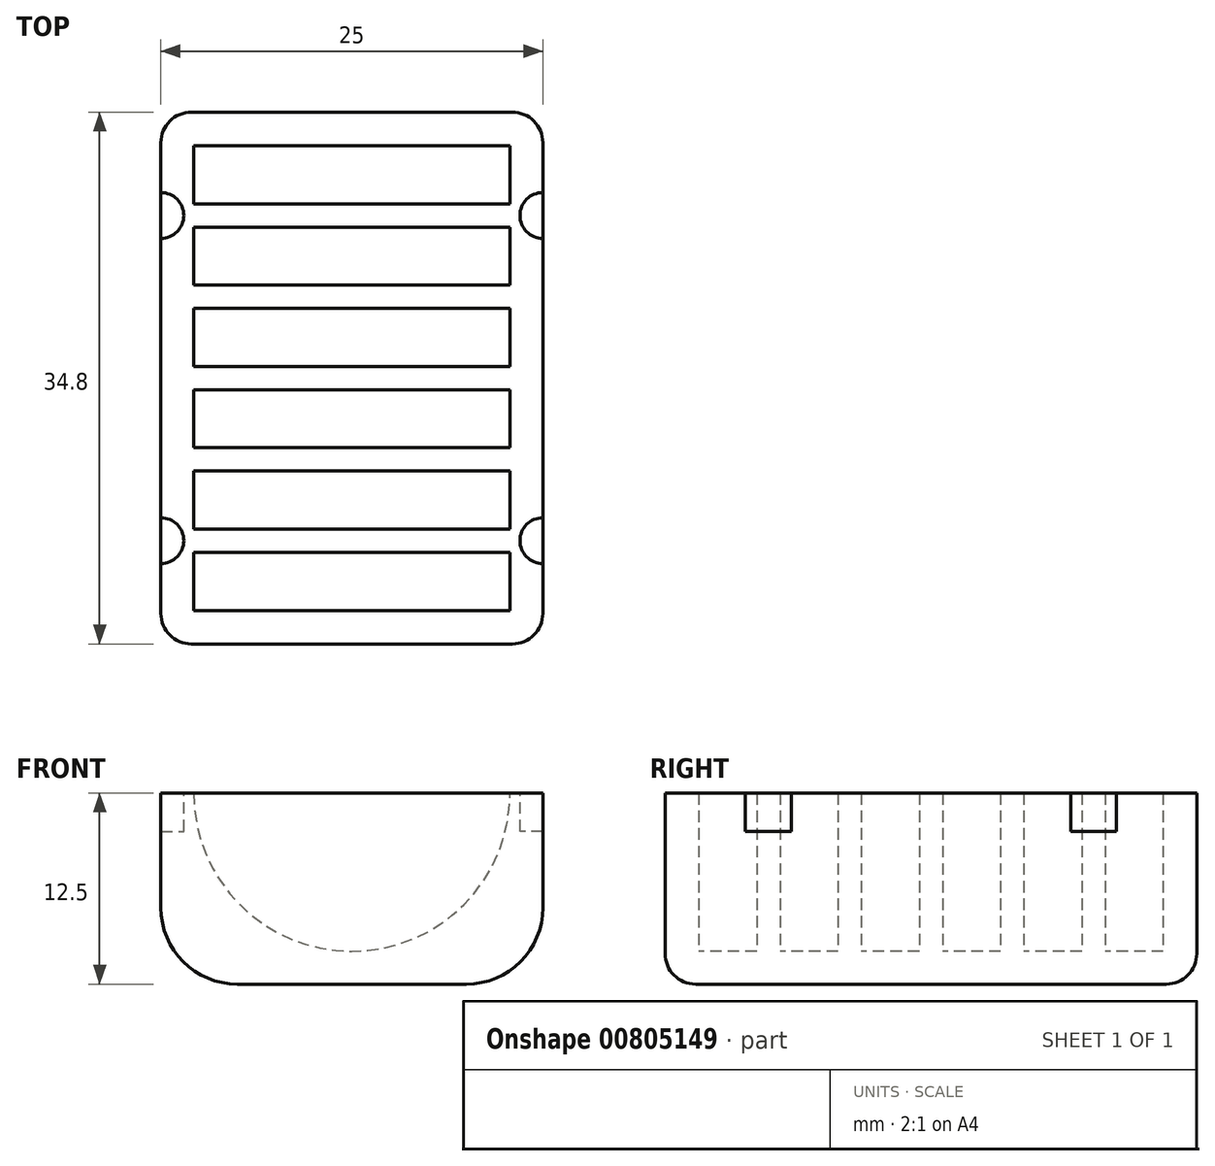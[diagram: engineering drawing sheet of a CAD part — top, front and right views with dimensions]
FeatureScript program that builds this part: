
annotation { "Feature Type Name" : "Feature", "Feature Type Description" : "" }
export const myFeature = defineFeature(function(context is Context, id is Id, definition is map)
    precondition{}
    {
        {
            var Q0;
            Q0=qCreatedBy(makeId("Top.planeOp"),FACE);
            var sketch = newSketch(context, id + "F0", { "sketchPlane" : qUnion([Q0])});
            skLineSegment(sketch, "E0.bottom", {"start": v(-30.1, 7.68) * mm, "end": v(-5.1, 7.68) * mm});
            skLineSegment(sketch, "E0.top", {"start": v(-30.1, -27.12) * mm, "end": v(-5.1, -27.12) * mm});
            skLineSegment(sketch, "E0.left", {"start": v(-30.1, 7.68) * mm, "end": v(-30.1, -27.12) * mm});
            skLineSegment(sketch, "E0.right", {"start": v(-5.1, 7.68) * mm, "end": v(-5.1, -27.12) * mm});
            skSolve(sketch);
        }
        {
            var Q0;
            Q0=qSketchRegion(id+"F0",true);
            extrude(context, id + "F1", {"entities" : qUnion([Q0]), "depth" : (25 / 2) * mm, "offsetDistance" : 25 * mm});
        }
        {
            var Q0;
            Q0=makeQuery(id+"F1.opExtrude","SWEPT_FACE",FACE,{"disambiguationData":[OSD([sQuery(id+"F0.wireOp",EDGE,"E0.top")])]});
            var sketch = newSketch(context, id + "F2", { "sketchPlane" : qUnion([Q0])});
            skCircle(sketch, "E1", {"center": v(-17.6, 12.5) * mm, "radius": 10.35 * mm});
            skSolve(sketch);
        }
        {
            var Q0;
            Q0=qSketchRegion(id+"F2",true);
            extrude(context, id + "F3", {"entities" : qUnion([Q0]), "operationType" : NewBodyOperationType.REMOVE, "oppositeDirection" : true, "depth" : (34.8 - 2.2) * mm, "offsetDistance" : 25 * mm, "hasSecondDirection" : true, "secondDirectionOppositeDirection" : true, "secondDirectionDepth" : (2.2) * mm});
        }
        {
            var Q0;
            Q0=makeQuery(id+"F1.opExtrude","CAP_FACE",FACE,{"disambiguationData":[OSD([sQuery(id+"F0.wireOp",EDGE,"E0.bottom"),sQuery(id+"F0.wireOp",EDGE,"E0.top"),sQuery(id+"F0.wireOp",EDGE,"E0.left"),sQuery(id+"F0.wireOp",EDGE,"E0.right")])],"isStart":false});
            var sketch = newSketch(context, id + "F4", { "sketchPlane" : qUnion([Q0])});
            skLineSegment(sketch, "E2.bottom", {"start": v(-27.95, 1.68) * mm, "end": v(-7.25, 1.68) * mm});
            skLineSegment(sketch, "E2.top", {"start": v(-27.95, 0.16) * mm, "end": v(-7.25, 0.16) * mm});
            skLineSegment(sketch, "E2.left", {"start": v(-27.95, 1.68) * mm, "end": v(-27.95, 0.16) * mm});
            skLineSegment(sketch, "E2.right", {"start": v(-7.25, 1.68) * mm, "end": v(-7.25, 0.16) * mm});
            skLineSegment(sketch, "E3.bottom", {"start": v(-27.95, -3.64) * mm, "end": v(-7.25, -3.64) * mm});
            skLineSegment(sketch, "E3.top", {"start": v(-27.95, -5.16) * mm, "end": v(-7.25, -5.16) * mm});
            skLineSegment(sketch, "E3.left", {"start": v(-27.95, -3.64) * mm, "end": v(-27.95, -5.16) * mm});
            skLineSegment(sketch, "E3.right", {"start": v(-7.25, -3.64) * mm, "end": v(-7.25, -5.16) * mm});
            skLineSegment(sketch, "E4.bottom", {"start": v(-27.95, -8.96) * mm, "end": v(-7.25, -8.96) * mm});
            skLineSegment(sketch, "E4.top", {"start": v(-27.95, -10.48) * mm, "end": v(-7.25, -10.48) * mm});
            skLineSegment(sketch, "E4.left", {"start": v(-27.95, -8.96) * mm, "end": v(-27.95, -10.48) * mm});
            skLineSegment(sketch, "E4.right", {"start": v(-7.25, -8.96) * mm, "end": v(-7.25, -10.48) * mm});
            skLineSegment(sketch, "E5.bottom", {"start": v(-27.95, -14.28) * mm, "end": v(-7.25, -14.28) * mm});
            skLineSegment(sketch, "E5.top", {"start": v(-27.95, -15.8) * mm, "end": v(-7.25, -15.8) * mm});
            skLineSegment(sketch, "E5.left", {"start": v(-27.95, -14.28) * mm, "end": v(-27.95, -15.8) * mm});
            skLineSegment(sketch, "E5.right", {"start": v(-7.25, -14.28) * mm, "end": v(-7.25, -15.8) * mm});
            skLineSegment(sketch, "E6.top", {"start": v(-27.95, -21.12) * mm, "end": v(-7.25, -21.12) * mm});
            skLineSegment(sketch, "E7", {"start": v(-27.95, -21.12) * mm, "end": v(-27.95, -19.6) * mm});
            skLineSegment(sketch, "E8", {"start": v(-27.95, -19.6) * mm, "end": v(-7.25, -19.6) * mm});
            skLineSegment(sketch, "E9", {"start": v(-7.25, -19.6) * mm, "end": v(-7.25, -21.12) * mm});
            skSolve(sketch);
        }
        {
            var Q0;
            Q0=qSketchRegion(id+"F4",true);
            extrude(context, id + "F5", {"entities" : qUnion([Q0]), "operationType" : NewBodyOperationType.ADD, "oppositeDirection" : true, "depth" : 10.6 * mm, "offsetDistance" : 25 * mm});
        }
        {
            var Q0;
            Q0=makeQuery(id+"F1.opExtrude","CAP_EDGE",EDGE,{"disambiguationData":[OSD([sQuery(id+"F0.wireOp",EDGE,"E0.right")])],"isStart":true});
            var Q1;
            Q1=makeQuery(id+"F1.opExtrude","CAP_EDGE",EDGE,{"disambiguationData":[OSD([sQuery(id+"F0.wireOp",EDGE,"E0.left")])],"isStart":true});
            fillet(context, id + "F6", {"entities" : qUnion([Q0, Q1]), "radius" : 5 * mm, "tangentPropagation" : true, "allowEdgeOverflow" : false});
        }
        {
            var Q0;
            Q0=makeQuery(id+"F1.opExtrude","SWEPT_EDGE",EDGE,{"disambiguationData":[OSD([sQuery(id+"F0.wireOp",EDGE,"E0.top"),sQuery(id+"F0.wireOp",EDGE,"E0.right")])]});
            var Q1;
            Q1=makeQuery(id+"F1.opExtrude","SWEPT_EDGE",EDGE,{"disambiguationData":[OSD([sQuery(id+"F0.wireOp",EDGE,"E0.bottom"),sQuery(id+"F0.wireOp",EDGE,"E0.right")])]});
            fillet(context, id + "F7", {"entities" : qUnion([Q0, Q1]), "radius" : 2 * mm, "tangentPropagation" : true, "allowEdgeOverflow" : false});
        }
        {
            var Q0;
            Q0=makeQuery(id+"F5.boolean.opBoolean","MERGE",FACE,{"derivedFrom":[makeQuery(id+"F1.opExtrude","CAP_FACE",FACE,{"disambiguationData":[OSD([sQuery(id+"F0.wireOp",EDGE,"E0.bottom"),sQuery(id+"F0.wireOp",EDGE,"E0.top"),sQuery(id+"F0.wireOp",EDGE,"E0.left"),sQuery(id+"F0.wireOp",EDGE,"E0.right")])],"isStart":false}),makeQuery(id+"F5.opExtrude","CAP_FACE",FACE,{"disambiguationData":[OSD([sQuery(id+"F4.wireOp",EDGE,"E2.bottom"),sQuery(id+"F4.wireOp",EDGE,"E2.top"),sQuery(id+"F4.wireOp",EDGE,"E2.left"),sQuery(id+"F4.wireOp",EDGE,"E2.right")])],"isStart":true}),makeQuery(id+"F5.opExtrude","CAP_FACE",FACE,{"disambiguationData":[OSD([sQuery(id+"F4.wireOp",EDGE,"E3.bottom"),sQuery(id+"F4.wireOp",EDGE,"E3.top"),sQuery(id+"F4.wireOp",EDGE,"E3.left"),sQuery(id+"F4.wireOp",EDGE,"E3.right")])],"isStart":true}),makeQuery(id+"F5.opExtrude","CAP_FACE",FACE,{"disambiguationData":[OSD([sQuery(id+"F4.wireOp",EDGE,"E4.bottom"),sQuery(id+"F4.wireOp",EDGE,"E4.top"),sQuery(id+"F4.wireOp",EDGE,"E4.left"),sQuery(id+"F4.wireOp",EDGE,"E4.right")])],"isStart":true}),makeQuery(id+"F5.opExtrude","CAP_FACE",FACE,{"disambiguationData":[OSD([sQuery(id+"F4.wireOp",EDGE,"E5.bottom"),sQuery(id+"F4.wireOp",EDGE,"E5.top"),sQuery(id+"F4.wireOp",EDGE,"E5.left"),sQuery(id+"F4.wireOp",EDGE,"E5.right")])],"isStart":true}),makeQuery(id+"F5.opExtrude","CAP_FACE",FACE,{"disambiguationData":[OSD([sQuery(id+"F4.wireOp",EDGE,"E6.top"),sQuery(id+"F4.wireOp",EDGE,"E7"),sQuery(id+"F4.wireOp",EDGE,"E8"),sQuery(id+"F4.wireOp",EDGE,"E9")])],"isStart":true})]});
            var sketch = newSketch(context, id + "F8", { "sketchPlane" : qUnion([Q0])});
            skCircle(sketch, "E10", {"center": v(-30.1, 0.92) * mm, "radius": 1.5 * mm});
            skCircle(sketch, "E11.1.0.0", {"center": v(-5.1, 0.92) * mm, "radius": 1.5 * mm});
            skCircle(sketch, "E12.MirrorC", {"center": v(-5.1, -20.36) * mm, "radius": 1.5 * mm});
            skCircle(sketch, "E13.MirrorC", {"center": v(-30.1, -20.36) * mm, "radius": 1.5 * mm});
            skSolve(sketch);
        }
        {
            var Q0;
            Q0=qSketchRegion(id+"F8",true);
            extrude(context, id + "F9", {"entities" : qUnion([Q0]), "operationType" : NewBodyOperationType.REMOVE, "oppositeDirection" : true, "depth" : 2.5 * mm, "offsetDistance" : 25 * mm});
        }
    });
